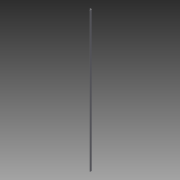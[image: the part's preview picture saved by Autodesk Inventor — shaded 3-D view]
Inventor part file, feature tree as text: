
AUTODESK INVENTOR PART (.ipt)
format: ipt  version: 2013 (Build 170138000, 138)  size: 85,504 bytes
history: native  units: in
note: dims shown in document units (in); Inventor stores cm internally (conversion verified against a paired STEP export)
features: other x2, extrude x1, sketch x1
ambient origin geometry x8: Origin, YZ Plane, XZ Plane, XY Plane, X Axis, Y Axis, Z Axis, Center Point
bodies: Solid1 (feature_tree)
feature tree (4):
  other  "Table"
  other  "Angle Iron-01"
  extrude  "Angle Iron Template"  Depth=1.0in
  sketch  "Sketch1"  dims[d2=0.1875in d3=1.0in d4=1.0in d5=0.1in d7=0.0in]
